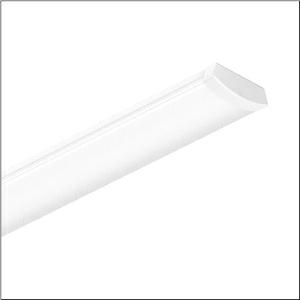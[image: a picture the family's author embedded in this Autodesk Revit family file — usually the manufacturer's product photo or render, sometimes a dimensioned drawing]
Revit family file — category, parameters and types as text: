
# Revit family: siluette_21_51ln12mkm40a3g
name_source: partatom
category: Lighting Fixtures
units: mm (PartAtom-declared; Revit-internal decimal feet)

## family parameters
Cut with Voids When Loaded = No
Host = Face
Light Source = No
Part Type = Normal
Room Calculation Point = No
Round Connector Dimension = Use Diameter
Shared = No

## types (1)
- --- (1 x LED, 2980 lm, 20.6 W, 5000K)
    Apparent Load = 21 VA
    CIE Flux Codes = 43 73 92 94 100
    Color Rendering = 80
    Color Temperature = 5000K
    Default Elevation = 1800 mm
    Description = Siluette 21, office luminaire, primary optical cover: enclosure, of PC, frosted, light emission: direct distribution, primary light characteristic: symmetric, installation type: suspended mounting, surface-mounted, LED, rated luminous flux: 5.010lm, luminous efficacy: 136lm/W, light colour: 830/840/850, colour temperature: 3000/4000/5000K, control gear: ON/OFF Multilumen, with terminal, 4-pole, mains connection: 220..240V, AC, 50/60Hz, rated input power: 37W, control gear: single battery element, housing, of sheet steel, white, length: 1.200mm, width: 152mm, height: 53mm, end cap, of PMMA, white, protection rating (complete): IP44, insulation class (complete): insulation class I (protective earthing), certification: CE, UKCA, protection symbol: D, impact resistance: IK04, permissible operating ambient temperature: +5..+40°C, standard: EN 60598-2-22, contact your sales advisor before using the luminaires in applications with unclear chemical exposure, large temperature fluctuations or condensation-forming humidity, corresponds to IFS (International Featured Standards) requirements for safety and quality in the food industry, packaging unit: 1 piece
    Height = 52 mm  [stored 0.170604 ft]
    Lamp = 1 x LED
    Lamp Light Flux = 2980 lm
    Lamp Power = 20.6 W
    Lamp count = 1
    Length = 1185 mm
    Luminous efficacy = 145 lm/W
    Manufacturer = Siteco
    ModVariant = No
    Model = 51LN12MKM40A3G
    Mounting Place = Ceiling
    Mounting Type = Pendant
    Number of Poles = 1
    OnlyDefault = Yes
    Power Factor = 1
    Product Name = Siluette 21
    Product group = office luminaire | ceiling pendant
    ProductGroupID = 903
    Protection Class = Protection class I
    Protection Degree = IP 44
    RLX_Detail_Level = 1
    RLX_Emergency_Light_Flux = 0 lm
    RLX_Emergency_Type = 0
    RLX_Emergency_Type_DB = No
    RlxData = <blob elided: 19517 chars, md5=85fc7970>
    Socket = socket
    Standby Power = 0 W
    System Light Flux = 2980 lm
    System Power = 21 W
    Type Comments = individual setting: colour temperature 5000K, luminous flux: 60 % | (OFF | OFF | ON) | 200 mA
    Type Image = l_1296910.jpg
    URL = http://relux.com
    VarID = @adj_067383
    Voltage = 0 V
    Weight = 0.00 kg
    Width = 152 mm

note: [stored X ft] marks values corroborated as IEEE doubles in the binary element streams (Revit-internal decimal feet)

## geometry (parser evidence)
native form markers: Blend x4, Sweep x12
no freeform markers — native parametric forms only
